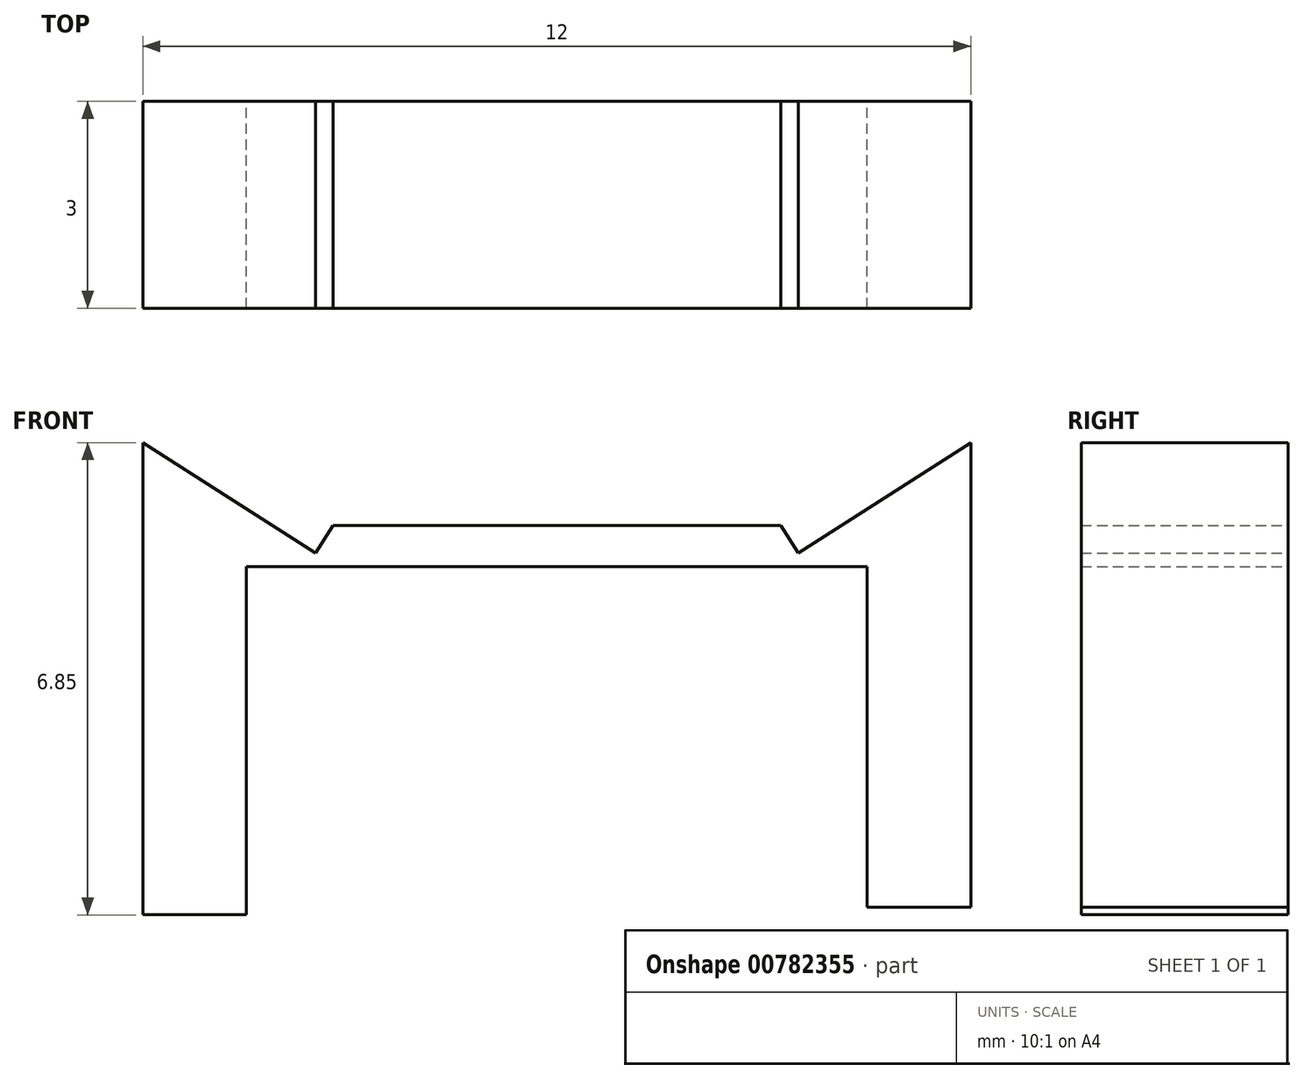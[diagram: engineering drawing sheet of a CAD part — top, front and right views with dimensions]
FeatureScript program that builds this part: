
annotation { "Feature Type Name" : "Feature", "Feature Type Description" : "" }
export const myFeature = defineFeature(function(context is Context, id is Id, definition is map)
    precondition{}
    {
        {
            var Q0;
            Q0=qCreatedBy(makeId("Front.planeOp"),FACE);
            var sketch = newSketch(context, id + "F0", { "sketchPlane" : qUnion([Q0])});
            skLineSegment(sketch, "E0", {"start": v(-6, 0) * mm, "end": v(-6, 1.8) * mm});
            skLineSegment(sketch, "E1", {"start": v(-6, 1.8) * mm, "end": v(-3.5, 0.2) * mm});
            skLineSegment(sketch, "E2", {"start": v(-3.5, 0.2) * mm, "end": v(-3.24, 0.6) * mm});
            skLineSegment(sketch, "E3", {"start": v(-3.24, 0.6) * mm, "end": v(3.24, 0.6) * mm});
            skLineSegment(sketch, "E4", {"start": v(3.24, 0.6) * mm, "end": v(3.5, 0.2) * mm});
            skLineSegment(sketch, "E5", {"start": v(3.5, 0.2) * mm, "end": v(6, 1.8) * mm});
            skLineSegment(sketch, "E6", {"start": v(6, 1.8) * mm, "end": v(6, 0) * mm});
            skLineSegment(sketch, "E7", {"start": v(4.5, 0) * mm, "end": v(-4.5, 0) * mm});
            skLineSegment(sketch, "E8", {"start": v(-4.5, 0) * mm, "end": v(-4.5, -5.05) * mm});
            skLineSegment(sketch, "E9", {"start": v(-4.5, -5.05) * mm, "end": v(-6, -5.05) * mm});
            skLineSegment(sketch, "E10", {"start": v(-6, -5.05) * mm, "end": v(-6, 0) * mm});
            skLineSegment(sketch, "E11", {"start": v(6, 0) * mm, "end": v(6, -4.94) * mm});
            skLineSegment(sketch, "E12", {"start": v(6, -4.94) * mm, "end": v(4.5, -4.94) * mm});
            skLineSegment(sketch, "E13", {"start": v(4.5, -4.94) * mm, "end": v(4.5, 0) * mm});
            skSolve(sketch);
        }
        {
            var Q0;
            Q0 = qSketchRegion(id + "F0", true);
            extrude(context, id + "F1", {"entities" : qUnion([Q0]), "endBound" : BoundingType.SYMMETRIC, "depth" : 3 * mm, "offsetDistance" : 25 * mm});
        }
    });
